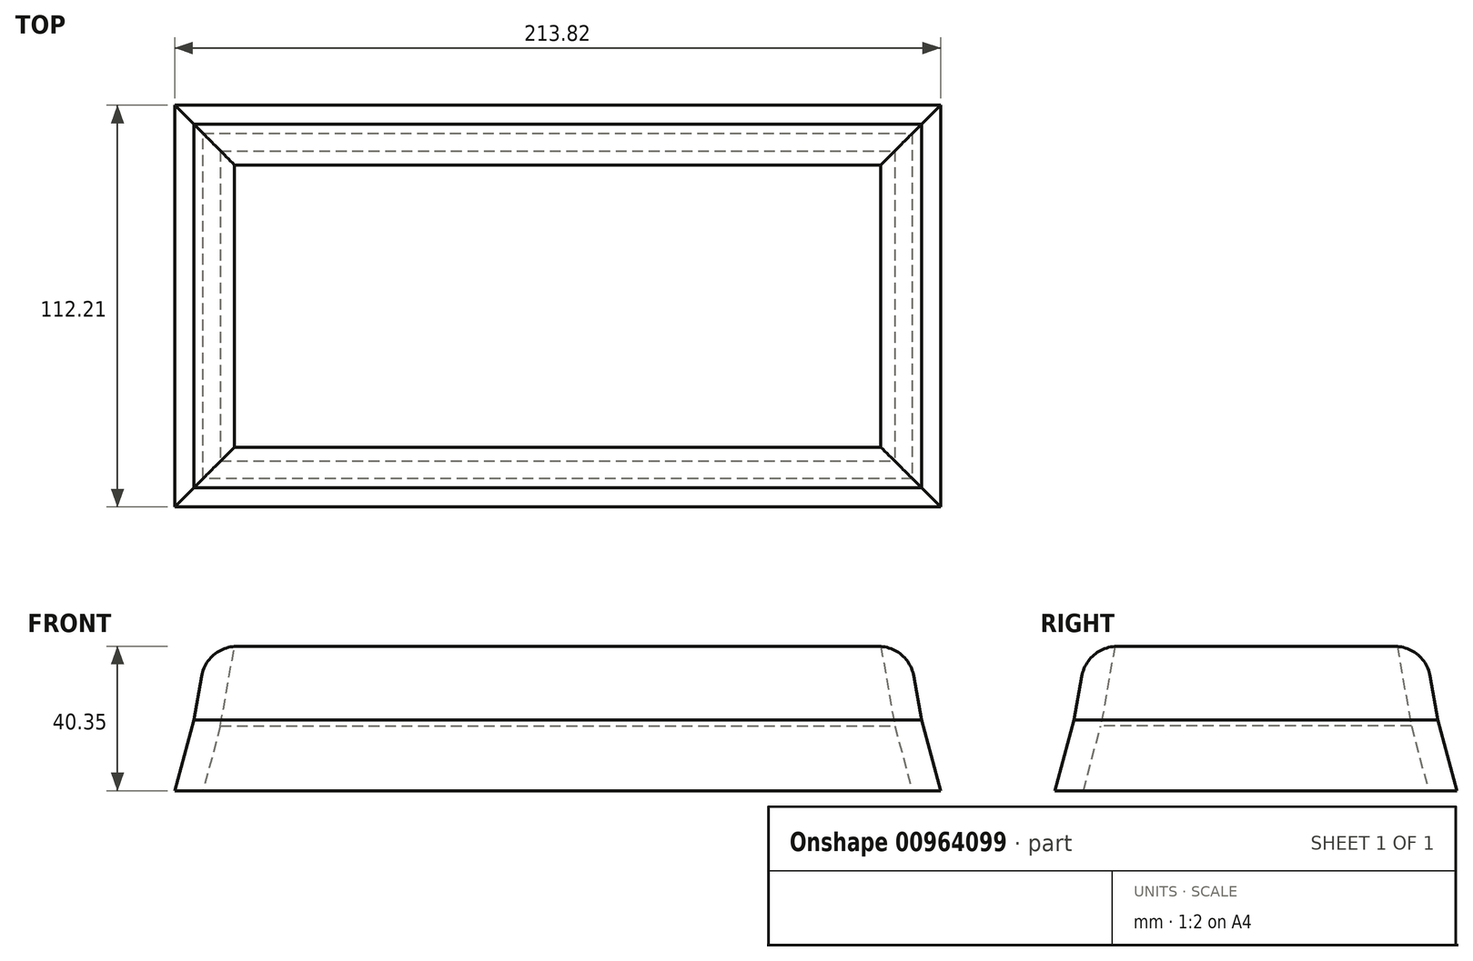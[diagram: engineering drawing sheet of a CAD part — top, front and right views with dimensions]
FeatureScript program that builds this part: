
annotation { "Feature Type Name" : "Feature", "Feature Type Description" : "" }
export const myFeature = defineFeature(function(context is Context, id is Id, definition is map)
    precondition{}
    {
        {
            var Q0;
            Q0=qCreatedBy(makeId("Top.planeOp"),FACE);
            var sketch = newSketch(context, id + "F0", { "sketchPlane" : qUnion([Q0])});
            skLineSegment(sketch, "E0.bottom", {"start": v(-101.1, 72.77) * mm, "end": v(102.1, 72.77) * mm});
            skLineSegment(sketch, "E0.top", {"start": v(-101.1, -28.83) * mm, "end": v(102.1, -28.83) * mm});
            skLineSegment(sketch, "E0.left", {"start": v(-101.1, 72.77) * mm, "end": v(-101.1, -28.83) * mm});
            skLineSegment(sketch, "E0.right", {"start": v(102.1, 72.77) * mm, "end": v(102.1, -28.83) * mm});
            skSolve(sketch);
        }
        {
            var Q0;
            Q0=makeQuery(id+"F0.imprint","IMPRINT",FACE,{"disambiguationData":[TD([[makeQuery(id+"F0.imprint","IMPRINT",EDGE,{"derivedFrom":sQuery(id+"F0.wireOp",EDGE,"E0.bottom")}),-1.0]])]});
            extrude(context, id + "F1", {"entities" : qUnion([Q0]), "depth" : 20.57 * mm, "offsetDistance" : 25.4 * mm, "hasDraft" : true, "draftAngle" : 10 * degree, "draftPullDirection" : true, "hasSecondDirection" : true, "secondDirectionOppositeDirection" : true, "secondDirectionDepth" : 19.8 * mm, "hasSecondDirectionDraft" : true, "secondDirectionDraftAngle" : 15 * degree});
        }
        {
            var Q0;
            Q0=makeQuery(id+"F1.opExtrude","CAP_FACE",FACE,{"disambiguationData":[OSD([sQuery(id+"F0.wireOp",EDGE,"E0.bottom"),sQuery(id+"F0.wireOp",EDGE,"E0.top"),sQuery(id+"F0.wireOp",EDGE,"E0.left"),sQuery(id+"F0.wireOp",EDGE,"E0.right")])],"isStart":false});
            var Q1;
            Q1=makeQuery(id+"F1.opExtrude","CAP_FACE",FACE,{"disambiguationData":[OSD([sQuery(id+"F0.wireOp",EDGE,"E0.bottom"),sQuery(id+"F0.wireOp",EDGE,"E0.top"),sQuery(id+"F0.wireOp",EDGE,"E0.left"),sQuery(id+"F0.wireOp",EDGE,"E0.right")])],"isStart":true});
            shell(context, id + "F2", {"entities" : qUnion([Q0, Q1]), "thickness" : 7.62 * mm});
        }
        {
            var Q0;
            Q0=makeQuery(id+"F1.opExtrude","CAP_EDGE",EDGE,{"disambiguationData":[OSD([sQuery(id+"F0.wireOp",EDGE,"E0.top")])],"isStart":false});
            var Q1;
            Q1=makeQuery(id+"F1.opExtrude","CAP_EDGE",EDGE,{"disambiguationData":[OSD([sQuery(id+"F0.wireOp",EDGE,"E0.left")])],"isStart":false});
            var Q2;
            Q2=makeQuery(id+"F1.opExtrude","CAP_EDGE",EDGE,{"disambiguationData":[OSD([sQuery(id+"F0.wireOp",EDGE,"E0.bottom")])],"isStart":false});
            var Q3;
            Q3=makeQuery(id+"F1.opExtrude","CAP_EDGE",EDGE,{"disambiguationData":[OSD([sQuery(id+"F0.wireOp",EDGE,"E0.right")])],"isStart":false});
            fillet(context, id + "F3", {"entities" : qUnion([Q0, Q1, Q2, Q3]), "radius" : 10.16 * mm, "tangentPropagation" : true, "allowEdgeOverflow" : false});
        }
    });
